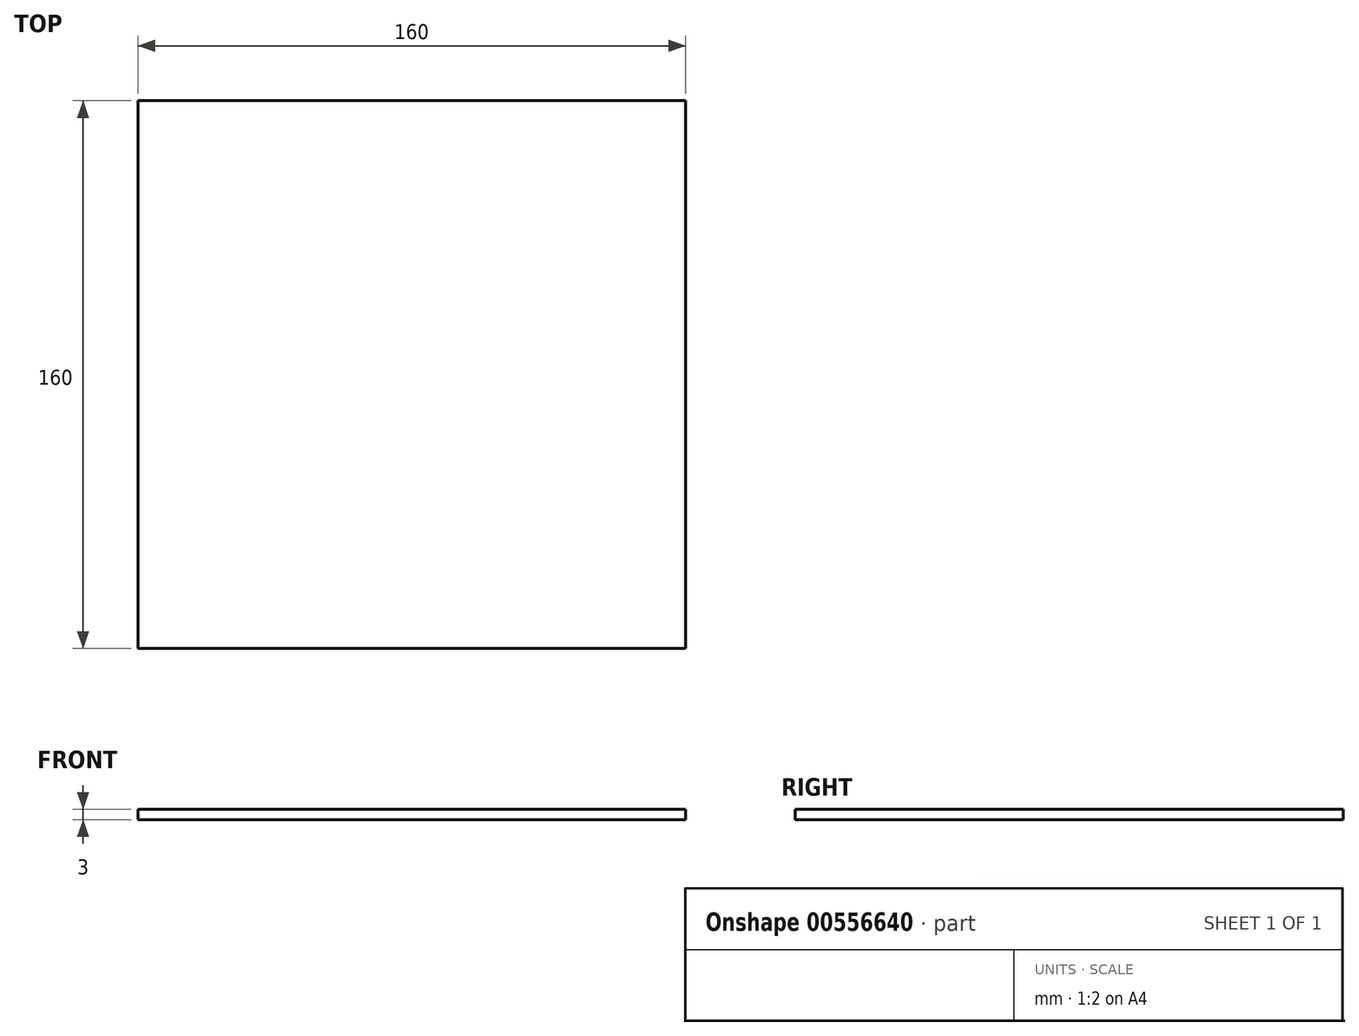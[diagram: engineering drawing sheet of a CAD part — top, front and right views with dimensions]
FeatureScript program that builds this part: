
annotation { "Feature Type Name" : "Feature", "Feature Type Description" : "" }
export const myFeature = defineFeature(function(context is Context, id is Id, definition is map)
    precondition{}
    {
        {
            var Q0;
            Q0=qCreatedBy(makeId("Top.planeOp"),FACE);
            var sketch = newSketch(context, id + "F0", { "sketchPlane" : qUnion([Q0])});
            skLineSegment(sketch, "E0", {"start": v(0, 0) * mm, "end": v(0, -160) * mm});
            skLineSegment(sketch, "E1", {"start": v(0, -160) * mm, "end": v(160, -160) * mm});
            skLineSegment(sketch, "E2", {"start": v(160, -160) * mm, "end": v(160, 0) * mm});
            skLineSegment(sketch, "E3", {"start": v(160, 0) * mm, "end": v(0, 0) * mm});
            skSolve(sketch);
        }
        {
            var Q0;
            Q0=makeQuery(id+"F0.imprint","IMPRINT",FACE,{"disambiguationData":[TD([[makeQuery(id+"F0.imprint","IMPRINT",EDGE,{"derivedFrom":sQuery(id+"F0.wireOp",EDGE,"E0")}),1.0]])]});
            extrude(context, id + "F1", {"entities" : qUnion([Q0]), "depth" : 3 * mm, "offsetDistance" : 25 * mm});
        }
    });
